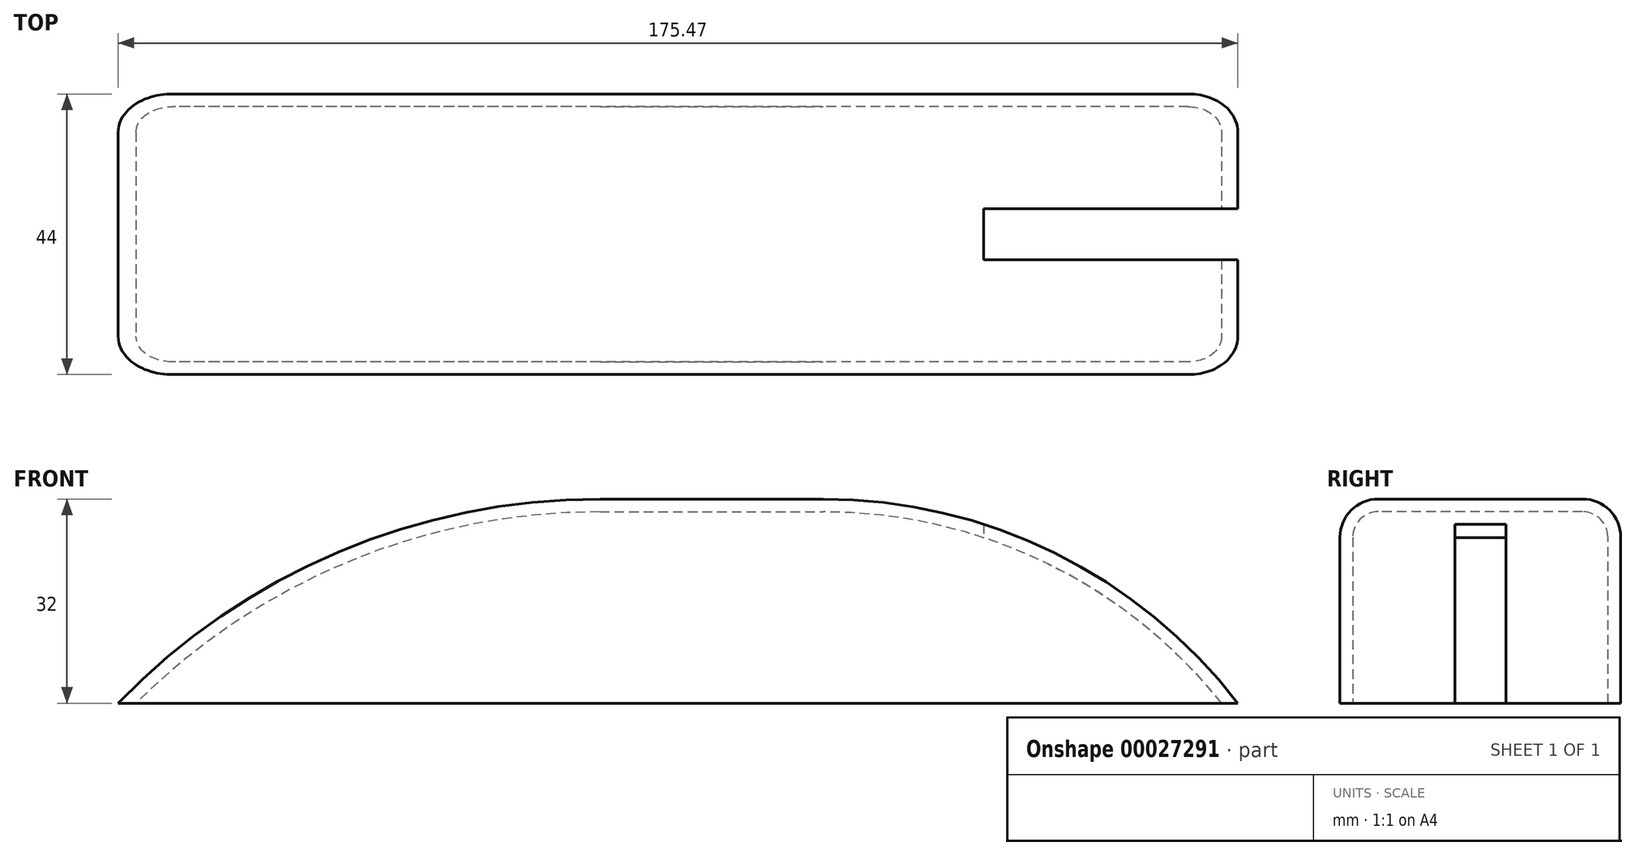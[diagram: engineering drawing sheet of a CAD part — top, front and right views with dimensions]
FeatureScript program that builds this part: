
annotation { "Feature Type Name" : "Feature", "Feature Type Description" : "" }
export const myFeature = defineFeature(function(context is Context, id is Id, definition is map)
    precondition{}
    {
        {
            var Q0;
            Q0=qCreatedBy(makeId("Top.planeOp"),FACE);
            var sketch = newSketch(context, id + "F0", { "sketchPlane" : qUnion([Q0])});
            skLineSegment(sketch, "E0.bottom", {"start": v(90, 22) * mm, "end": v(-90, 22) * mm});
            skLineSegment(sketch, "E0.top", {"start": v(90, -22) * mm, "end": v(-90, -22) * mm});
            skLineSegment(sketch, "E0.left", {"start": v(90, 22) * mm, "end": v(90, -22) * mm});
            skLineSegment(sketch, "E0.right", {"start": v(-90, 22) * mm, "end": v(-90, -22) * mm});
            skPoint(sketch, "E0.middle", {"position": v(0, 0) * mm});
            skSolve(sketch);
        }
        {
            var Q0;
            Q0=qSketchRegion(id+"F0",true);
            extrude(context, id + "F1", {"entities" : qUnion([Q0]), "depth" : 37 * mm});
        }
        {
            var Q0;
            Q0=makeQuery(id+"F1.opExtrude","SWEPT_FACE",FACE,{"disambiguationData":[OSD([sQuery(id+"F0.wireOp",EDGE,"E0.left")])]});
            var sketch = newSketch(context, id + "F2", { "sketchPlane" : qUnion([Q0])});
            skLineSegment(sketch, "E1", {"start": v(0, 0) * mm, "end": v(0, 50.8) * mm});
            skCircle(sketch, "E2", {"center": v(0, 50.8) * mm, "radius": 11.5 * mm});
            skCircle(sketch, "E3", {"center": v(0, 50.8) * mm, "radius": 50.8 * mm, "construction": true});
            skSolve(sketch);
        }
        {
            var Q0;
            Q0=qCreatedBy(makeId("Front.planeOp"),FACE);
            var sketch = newSketch(context, id + "F3", { "sketchPlane" : qUnion([Q0])});
            skLineSegment(sketch, "E4.0", {"start": v(90, 0) * mm, "end": v(90, 50.8) * mm});
            skLineSegment(sketch, "E5.0", {"start": v(-90, 37) * mm, "end": v(-90, 0) * mm});
            skLineSegment(sketch, "E6.0", {"start": v(90, 37) * mm, "end": v(-90, 37) * mm});
            skArc(sketch, "E7", {"start": v(-10, 37) * mm, "mid": v(-54.07, 27.3) * mm, "end": v(-90, 0) * mm});
            skLineSegment(sketch, "E8", {"start": v(0, 37) * mm, "end": v(0, 0) * mm, "construction": true});
            skArc(sketch, "E9", {"start": v(90, 5) * mm, "mid": v(61.22, 28.57) * mm, "end": v(25, 37) * mm});
            skSolve(sketch);
        }
        {
            var Q0;
            Q0=qSketchRegion(id+"F3",true);
            extrude(context, id + "F4", {"entities" : qUnion([Q0]), "operationType" : NewBodyOperationType.REMOVE, "oppositeDirection" : true, "depth" : 25 * mm, "hasSecondDirection" : true, "secondDirectionOppositeDirection" : false, "secondDirectionDepth" : 25 * mm});
        }
        {
            var Q0;
            Q0=qCreatedBy(makeId("Front.planeOp"),FACE);
            var sketch = newSketch(context, id + "F5", { "sketchPlane" : qUnion([Q0])});
            skLineSegment(sketch, "E10.top", {"start": v(48, 32) * mm, "end": v(-32, 32) * mm});
            skLineSegment(sketch, "E10.right", {"start": v(-32, 2) * mm, "end": v(-32, 32) * mm});
            skLineSegment(sketch, "E11", {"start": v(48, 32) * mm, "end": v(48, 2) * mm});
            skLineSegment(sketch, "E12", {"start": v(48, 2) * mm, "end": v(-32, 2) * mm});
            skSolve(sketch);
        }
        {
            var Q0;
            Q0=qSketchRegion(id+"F5",true);
            extrude(context, id + "F6", {"entities" : qUnion([Q0]), "depth" : (35 / 2) * mm, "hasSecondDirection" : true, "secondDirectionOppositeDirection" : true, "secondDirectionDepth" : 17.5 * mm});
        }
        {
            var Q0;
            Q0=makeQuery(id+"F4.boolean.opBoolean","INTERSECT",EDGE,{"derivedFrom":[makeQuery(id+"F1.opExtrude","SWEPT_FACE",FACE,{"disambiguationData":[OSD([sQuery(id+"F0.wireOp",EDGE,"E0.bottom")])]}),makeQuery(id+"F4.opExtrude","SWEPT_FACE",FACE,{"disambiguationData":[OSD([sQuery(id+"F3.wireOp",EDGE,"E7")])]})]});
            var Q1;
            Q1=makeQuery(id+"F1.opExtrude","CAP_EDGE",EDGE,{"disambiguationData":[OSD([sQuery(id+"F0.wireOp",EDGE,"E0.bottom")])],"isStart":false});
            var Q2;
            Q2=makeQuery(id+"F4.boolean.opBoolean","INTERSECT",EDGE,{"derivedFrom":[makeQuery(id+"F1.opExtrude","SWEPT_FACE",FACE,{"disambiguationData":[OSD([sQuery(id+"F0.wireOp",EDGE,"E0.top")])]}),makeQuery(id+"F4.opExtrude","SWEPT_FACE",FACE,{"disambiguationData":[OSD([sQuery(id+"F3.wireOp",EDGE,"E7")])]})]});
            var Q3;
            Q3=makeQuery(id+"F4.boolean.opBoolean","INTERSECT",EDGE,{"derivedFrom":[makeQuery(id+"F1.opExtrude","SWEPT_FACE",FACE,{"disambiguationData":[OSD([sQuery(id+"F0.wireOp",EDGE,"E0.bottom")])]}),makeQuery(id+"F4.opExtrude","SWEPT_FACE",FACE,{"disambiguationData":[OSD([sQuery(id+"F3.wireOp",EDGE,"E9")])]})]});
            fillet(context, id + "F7", {"entities" : qUnion([Q0, Q1, Q2, Q3]), "radius" : 6 * mm, "tangentPropagation" : true, "allowEdgeOverflow" : false});
        }
        {
            var Q0;
            {var subQ1=sQuery(id+"F0.wireOp",EDGE,"E0.left");var subQ6=makeQuery(id+"F1.opExtrude","SWEPT_EDGE",EDGE,{"disambiguationData":[OSD([sQuery(id+"F0.wireOp",EDGE,"E0.top"),subQ1])]});Q0=makeQuery(id+"F2.imprint","IMPRINT",FACE,{"disambiguationData":[TD([[makeQuery(id+"F2.imprint","IMPRINT",EDGE,{"derivedFrom":subQ6}),1.0]])]});}
            var sketch = newSketch(context, id + "F8", { "sketchPlane" : qUnion([Q0])});
            skLineSegment(sketch, "E13.bottom", {"start": v(-3, 50.8) * mm, "end": v(3, 50.8) * mm});
            skLineSegment(sketch, "E13.top", {"start": v(-3, 0) * mm, "end": v(3, 0) * mm});
            skLineSegment(sketch, "E13.left", {"start": v(-3, 50.8) * mm, "end": v(-3, 0) * mm});
            skLineSegment(sketch, "E13.right", {"start": v(3, 50.8) * mm, "end": v(3, 0) * mm});
            skPoint(sketch, "E13.middle", {"position": v(0, 25.4) * mm});
            skLineSegment(sketch, "E14.0", {"start": v(0, 0) * mm, "end": v(0, 50.8) * mm, "construction": true});
            skSolve(sketch);
        }
        {
            var Q0;
            Q0=qSketchRegion(id+"F8",true);
            var Q1;
            Q1=sQuery(id+"F8.wireOp",EDGE,"E13.top");
            revolve(context, id + "F9", {"operationType" : NewBodyOperationType.ADD, "entities" : qUnion([Q0]), "axis" : qUnion([Q1]), "revolveType" : RevolveType.ONE_DIRECTION, "oppositeDirection" : true, "angle" : 56 * degree});
        }
        {
            var Q0;
            Q0=makeQuery(id+"F2.imprint","IMPRINT",FACE,{"disambiguationData":[TD([[makeQuery(id+"F2.imprint","IMPRINT",EDGE,{"derivedFrom":sQuery(id+"F2.wireOp",EDGE,"E2")}),1.0]])]});
            var sketch = newSketch(context, id + "F10", { "sketchPlane" : qUnion([Q0])});
            skCircle(sketch, "E15.0", {"center": v(0, 50.8) * mm, "radius": 11.5 * mm, "construction": true});
            skCircle(sketch, "E16.0", {"center": v(0, 50.8) * mm, "radius": 12.5 * mm});
            skSolve(sketch);
        }
        {
            var Q0;
            Q0=qSketchRegion(id+"F10",true);
            extrude(context, id + "F11", {"entities" : qUnion([Q0]), "operationType" : NewBodyOperationType.REMOVE, "oppositeDirection" : true, "depth" : 14 * mm});
        }
        {
            var Q0;
            Q0=qCreatedBy(makeId("Front.planeOp"),FACE);
            var sketch = newSketch(context, id + "F12", { "sketchPlane" : qUnion([Q0])});
            skPoint(sketch, "E17.0", {"position": v(90, 50.8) * mm});
            skLineSegment(sketch, "E18", {"start": v(90, 50.8) * mm, "end": v(60, 50.8) * mm});
            skLineSegment(sketch, "E19", {"start": v(73, 50.8) * mm, "end": v(73, 38.3) * mm, "construction": true});
            skArc(sketch, "E20", {"start": v(60, 50.8) * mm, "mid": v(65.54, 43.55) * mm, "end": v(73, 38.3) * mm});
            skLineSegment(sketch, "E21.0", {"start": v(76, 38.3) * mm, "end": v(76, 50.8) * mm});
            skPoint(sketch, "E22.orphan", {"position": v(76, 48.83) * mm});
            skLineSegment(sketch, "E23", {"start": v(73, 38.3) * mm, "end": v(76, 38.3) * mm});
            skPoint(sketch, "E24.orphan", {"position": v(76, 38.67) * mm});
            skSolve(sketch);
        }
        {
            var Q0;
            Q0=qSketchRegion(id+"F12",true);
            var Q1;
            Q1=sQuery(id+"F12.wireOp",EDGE,"E18");
            revolve(context, id + "F13", {"operationType" : NewBodyOperationType.ADD, "entities" : qUnion([Q0]), "axis" : qUnion([Q1]), "revolveType" : RevolveType.FULL});
        }
        {
            var Q0;
            Q0=makeQuery(id+"F13.boolean.opBoolean","MERGE",FACE,{"derivedFrom":[makeQuery(id+"F11.boolean.opBoolean","COPY",FACE,{"derivedFrom":makeQuery(id+"F11.opExtrude","CAP_FACE",FACE,{"disambiguationData":[OSD([sQuery(id+"F10.wireOp",EDGE,"E16.0")])],"isStart":false})}),makeQuery(id+"F13.opRevolve","SWEPT_FACE",FACE,{"disambiguationData":[OSD([sQuery(id+"F12.wireOp",EDGE,"E21.0")])]})]});
            var sketch = newSketch(context, id + "F14", { "sketchPlane" : qUnion([Q0])});
            skLineSegment(sketch, "E25", {"start": v(5.66, 45.14) * mm, "end": v(-5.66, 56.46) * mm, "construction": true});
            skLineSegment(sketch, "E26", {"start": v(4.24, 55.04) * mm, "end": v(-4.24, 46.56) * mm, "construction": true});
            skCircle(sketch, "E27", {"center": v(-5.66, 56.46) * mm, "radius": 1 * mm});
            skCircle(sketch, "E28", {"center": v(4.24, 55.04) * mm, "radius": 1 * mm});
            skCircle(sketch, "E29", {"center": v(-4.24, 46.56) * mm, "radius": 1 * mm});
            skCircle(sketch, "E30", {"center": v(5.66, 45.14) * mm, "radius": 1 * mm});
            skSolve(sketch);
        }
        {
            var Q0;
            Q0=qSketchRegion(id+"F14",true);
            extrude(context, id + "F15", {"entities" : qUnion([Q0]), "operationType" : NewBodyOperationType.REMOVE, "endBound" : BoundingType.THROUGH_ALL, "oppositeDirection" : true, "depth" : 25 * mm});
        }
        {
            var Q0;
            Q0=makeQuery(id+"F13.boolean.opBoolean","MERGE",FACE,{"derivedFrom":[makeQuery(id+"F11.boolean.opBoolean","COPY",FACE,{"derivedFrom":makeQuery(id+"F11.opExtrude","CAP_FACE",FACE,{"disambiguationData":[OSD([sQuery(id+"F10.wireOp",EDGE,"E16.0")])],"isStart":false})}),makeQuery(id+"F13.opRevolve","SWEPT_FACE",FACE,{"disambiguationData":[OSD([sQuery(id+"F12.wireOp",EDGE,"E21.0")])]})]});
            var sketch = newSketch(context, id + "F16", { "sketchPlane" : qUnion([Q0])});
            skCircle(sketch, "E31", {"center": v(0, 50.8) * mm, "radius": 3 * mm});
            skSolve(sketch);
        }
        {
            var Q0;
            Q0=qSketchRegion(id+"F16",true);
            extrude(context, id + "F17", {"entities" : qUnion([Q0]), "operationType" : NewBodyOperationType.REMOVE, "oppositeDirection" : true, "depth" : 3 * mm});
        }
        {
            var Q0;
            Q0=makeQuery(id+"F17.boolean.opBoolean","COPY",EDGE,{"derivedFrom":makeQuery(id+"F17.opExtrude","CAP_EDGE",EDGE,{"disambiguationData":[OSD([sQuery(id+"F16.wireOp",EDGE,"E31")])],"isStart":false})});
            fillet(context, id + "F18", {"entities" : qUnion([Q0]), "radius" : 3 * mm, "tangentPropagation" : true, "allowEdgeOverflow" : false});
        }
        {
            var Q0;
            Q0=makeQuery(id+"F13.boolean.opBoolean","MERGE",FACE,{"derivedFrom":[makeQuery(id+"F11.boolean.opBoolean","COPY",FACE,{"derivedFrom":makeQuery(id+"F11.opExtrude","CAP_FACE",FACE,{"disambiguationData":[OSD([sQuery(id+"F10.wireOp",EDGE,"E16.0")])],"isStart":false})}),makeQuery(id+"F13.opRevolve","SWEPT_FACE",FACE,{"disambiguationData":[OSD([sQuery(id+"F12.wireOp",EDGE,"E21.0")])]})]});
            var sketch = newSketch(context, id + "F19", { "sketchPlane" : qUnion([Q0])});
            skCircle(sketch, "E32", {"center": v(-5.66, 56.46) * mm, "radius": 1.75 * mm});
            skCircle(sketch, "E33", {"center": v(4.24, 55.04) * mm, "radius": 1.75 * mm});
            skCircle(sketch, "E34", {"center": v(5.66, 45.14) * mm, "radius": 1.75 * mm});
            skCircle(sketch, "E35", {"center": v(-4.24, 46.56) * mm, "radius": 1.75 * mm});
            skSolve(sketch);
        }
        {
            var Q0;
            Q0=qSketchRegion(id+"F19",true);
            extrude(context, id + "F20", {"entities" : qUnion([Q0]), "operationType" : NewBodyOperationType.REMOVE, "endBound" : BoundingType.THROUGH_ALL, "oppositeDirection" : true, "depth" : 6.3 * mm, "hasSecondDirection" : true, "secondDirectionOppositeDirection" : true, "secondDirectionDepth" : 3 * mm});
        }
        {
            var Q0;
            Q0=qCreatedBy(makeId("Top.planeOp"),FACE);
            var sketch = newSketch(context, id + "F21", { "sketchPlane" : qUnion([Q0])});
            skLineSegment(sketch, "E36.0", {"start": v(51.14, -3) * mm, "end": v(51.14, 3) * mm});
            skLineSegment(sketch, "E37.0", {"start": v(51.14, -3) * mm, "end": v(90, -3) * mm});
            skLineSegment(sketch, "E38.0", {"start": v(51.14, 3) * mm, "end": v(90, 3) * mm});
            skLineSegment(sketch, "E39.0", {"start": v(50.14, -4) * mm, "end": v(90, -4) * mm});
            skLineSegment(sketch, "E39.1", {"start": v(50.14, -4) * mm, "end": v(50.14, 4) * mm});
            skLineSegment(sketch, "E39.2", {"start": v(50.14, 4) * mm, "end": v(90, 4) * mm});
            skLineSegment(sketch, "E40", {"start": v(90, -4) * mm, "end": v(90, 4) * mm});
            skSolve(sketch);
        }
        {
            var Q0;
            Q0=makeQuery(id+"F9.opRevolve","SWEPT_FACE",FACE,{"disambiguationData":[OSD([sQuery(id+"F8.wireOp",EDGE,"E13.left")])]});
            var sketch = newSketch(context, id + "F22", { "sketchPlane" : qUnion([Q0])});
            skArc(sketch, "E41.0.2", {"start": v(55.24, 37.05) * mm, "mid": v(53.13, 34.95) * mm, "end": v(51.14, 32.72) * mm});
            skArc(sketch, "E41.0.3", {"start": v(51.14, 32.72) * mm, "mid": v(72.63, 21.75) * mm, "end": v(90, 5) * mm});
            skLineSegment(sketch, "E41.0.4", {"start": v(90, 5) * mm, "end": v(90, 38.67) * mm});
            skLineSegment(sketch, "E42.bottom", {"start": v(46.63, 74.86) * mm, "end": v(104.26, 74.86) * mm});
            skLineSegment(sketch, "E42.top", {"start": v(46.63, 37.05) * mm, "end": v(55.24, 37.05) * mm});
            skLineSegment(sketch, "E42.left", {"start": v(46.63, 74.86) * mm, "end": v(46.63, 37.05) * mm});
            skLineSegment(sketch, "E42.right", {"start": v(104.26, 74.86) * mm, "end": v(104.26, 37.05) * mm});
            skLineSegment(sketch, "E43.trimOffspring", {"start": v(90, 37.05) * mm, "end": v(104.26, 37.05) * mm});
            skPoint(sketch, "E44.orphan", {"position": v(65.34, 44.41) * mm});
            skPoint(sketch, "E41.0.0.end.orphan", {"position": v(73, 38.67) * mm});
            skPoint(sketch, "E41.0.0.start.orphan", {"position": v(76, 38.67) * mm});
            skSolve(sketch);
        }
        {
            var Q0;
            Q0 = qSketchRegion(id + "F22", true);
            extrude(context, id + "F23", {"entities" : qUnion([Q0]), "operationType" : NewBodyOperationType.REMOVE, "endBound" : BoundingType.THROUGH_ALL, "depth" : 25 * mm, "hasSecondDirection" : true, "secondDirectionOppositeDirection" : true, "secondDirectionDepth" : 25 * mm});
        }
        {
            var Q0;
            Q0=makeQuery(id+"F1.opExtrude","CAP_FACE",FACE,{"disambiguationData":[OSD([sQuery(id+"F0.wireOp",EDGE,"E0.bottom"),sQuery(id+"F0.wireOp",EDGE,"E0.top"),sQuery(id+"F0.wireOp",EDGE,"E0.left"),sQuery(id+"F0.wireOp",EDGE,"E0.right")])],"isStart":true});
            extrude(context, id + "F24", {"entities" : qUnion([Q0]), "operationType" : NewBodyOperationType.REMOVE, "oppositeDirection" : true, "depth" : 5 * mm});
        }
        {
            var Q0;
            Q0=makeQuery(id+"F24.boolean.opBoolean","COPY",FACE,{"derivedFrom":makeQuery(id+"F24.opExtrude","CAP_FACE",FACE,{"disambiguationData":[OSD([sQuery(id+"F0.wireOp",EDGE,"E0.bottom"),sQuery(id+"F0.wireOp",EDGE,"E0.top"),sQuery(id+"F0.wireOp",EDGE,"E0.left"),sQuery(id+"F0.wireOp",EDGE,"E0.right")])],"isStart":false})});
            shell(context, id + "F25", {"entities" : qUnion([Q0]), "thickness" : 2 * mm});
        }
        {
            var Q0;
            Q0 = qSketchRegion(id + "F21", true);
            extrude(context, id + "F26", {"entities" : qUnion([Q0]), "operationType" : NewBodyOperationType.REMOVE, "endBound" : BoundingType.THROUGH_ALL, "depth" : 25 * mm});
        }
    });
